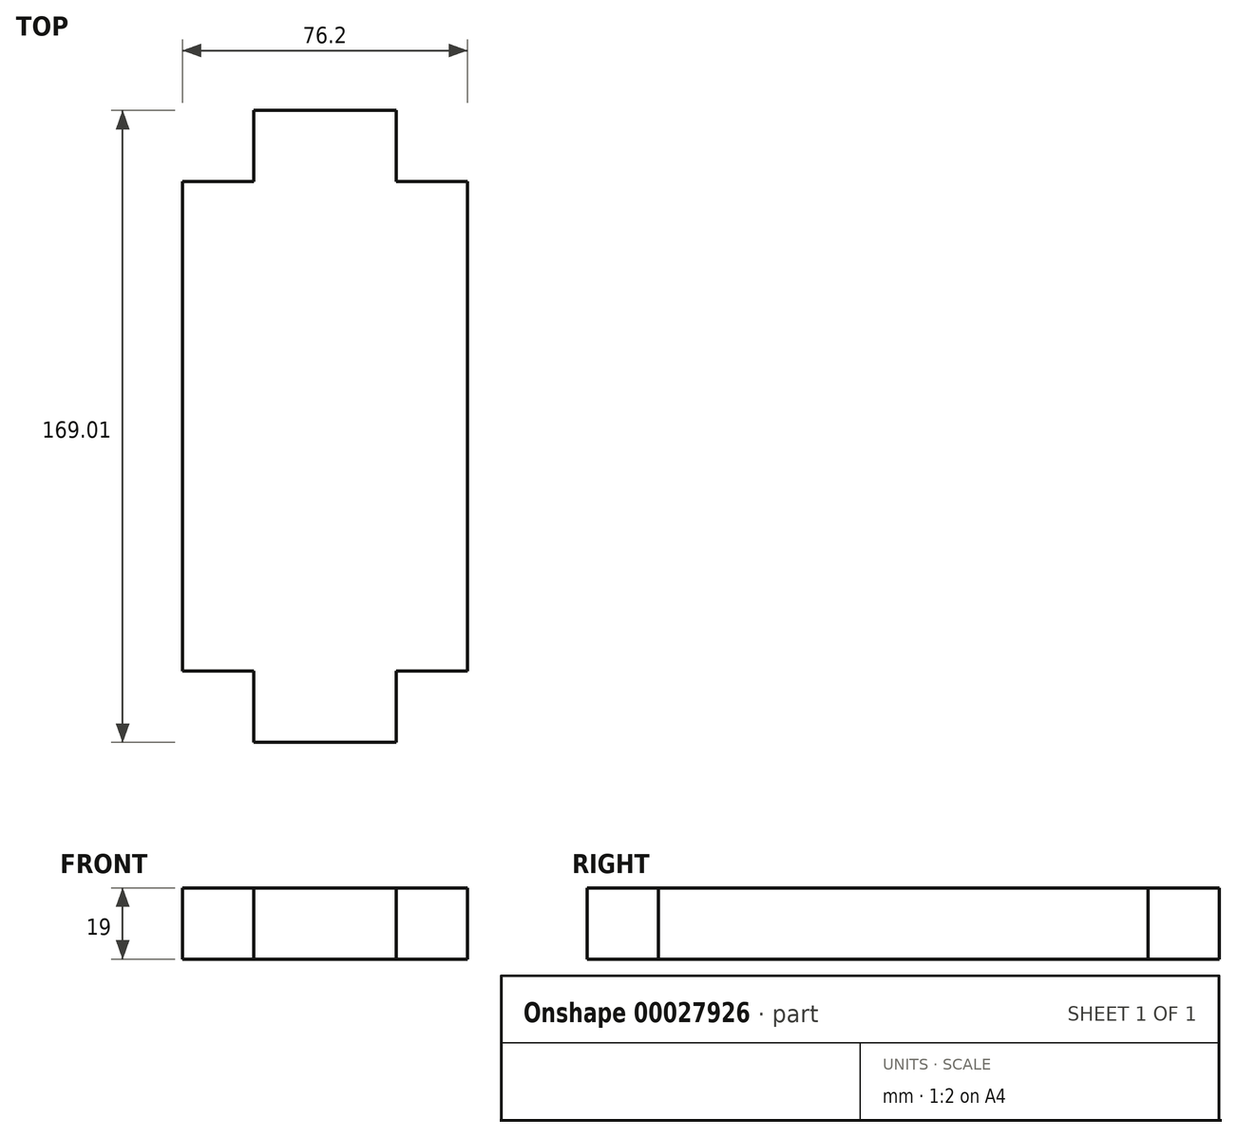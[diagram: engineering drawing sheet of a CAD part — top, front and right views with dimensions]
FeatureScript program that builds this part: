
annotation { "Feature Type Name" : "Feature", "Feature Type Description" : "" }
export const myFeature = defineFeature(function(context is Context, id is Id, definition is map)
    precondition{}
    {
        {
            var Q0;
            Q0=qCreatedBy(makeId("Right.planeOp"),FACE);
            var sketch = newSketch(context, id + "F0", { "sketchPlane" : qUnion([Q0])});
            skLineSegment(sketch, "E0", {"start": v(0, 0) * mm, "end": v(-131.01, 0) * mm});
            skLineSegment(sketch, "E1", {"start": v(0, 0) * mm, "end": v(0, -19) * mm});
            skLineSegment(sketch, "E2", {"start": v(0, -19) * mm, "end": v(-131.01, -19) * mm});
            skLineSegment(sketch, "E3", {"start": v(-131.01, -19) * mm, "end": v(-131.01, 0) * mm});
            skSolve(sketch);
        }
        {
            var Q0;
            Q0=qSketchRegion(id+"F0",true);
            extrude(context, id + "F1", {"entities" : qUnion([Q0]), "depth" : 76.2 * mm});
        }
        {
            var Q0;
            Q0=makeQuery(id+"F1.opExtrude","SWEPT_FACE",FACE,{"disambiguationData":[OSD([sQuery(id+"F0.wireOp",EDGE,"E1")])]});
            var sketch = newSketch(context, id + "F2", { "sketchPlane" : qUnion([Q0])});
            skLineSegment(sketch, "E4", {"start": v(-57.15, 0) * mm, "end": v(-57.15, -19) * mm});
            skLineSegment(sketch, "E5", {"start": v(-19.05, 0) * mm, "end": v(-19.05, -19) * mm});
            skSolve(sketch);
        }
        {
            var Q0;
            {var subQ3=sQuery(id+"F2.wireOp",EDGE,"E4");Q0=makeQuery(id+"F2.imprint","IMPRINT",FACE,{"disambiguationData":[TD([[makeQuery(id+"F2.imprint","IMPRINT",EDGE,{"derivedFrom":subQ3}),1.0]])]});}
            extrude(context, id + "F3", {"entities" : qUnion([Q0]), "operationType" : NewBodyOperationType.ADD, "depth" : 19 * mm});
        }
        {
            var Q0;
            Q0=makeQuery(id+"F1.opExtrude","SWEPT_FACE",FACE,{"disambiguationData":[OSD([sQuery(id+"F0.wireOp",EDGE,"E3")])]});
            var sketch = newSketch(context, id + "F4", { "sketchPlane" : qUnion([Q0])});
            skLineSegment(sketch, "E6", {"start": v(19.05, 0) * mm, "end": v(19.05, -19) * mm});
            skLineSegment(sketch, "E7", {"start": v(57.15, 0) * mm, "end": v(57.15, -19) * mm});
            skSolve(sketch);
        }
        {
            var Q0;
            {var subQ3=sQuery(id+"F4.wireOp",EDGE,"E6");Q0=makeQuery(id+"F4.imprint","IMPRINT",FACE,{"disambiguationData":[TD([[makeQuery(id+"F4.imprint","IMPRINT",EDGE,{"derivedFrom":subQ3}),1.0]])]});}
            extrude(context, id + "F5", {"entities" : qUnion([Q0]), "operationType" : NewBodyOperationType.ADD, "depth" : 19 * mm});
        }
    });
